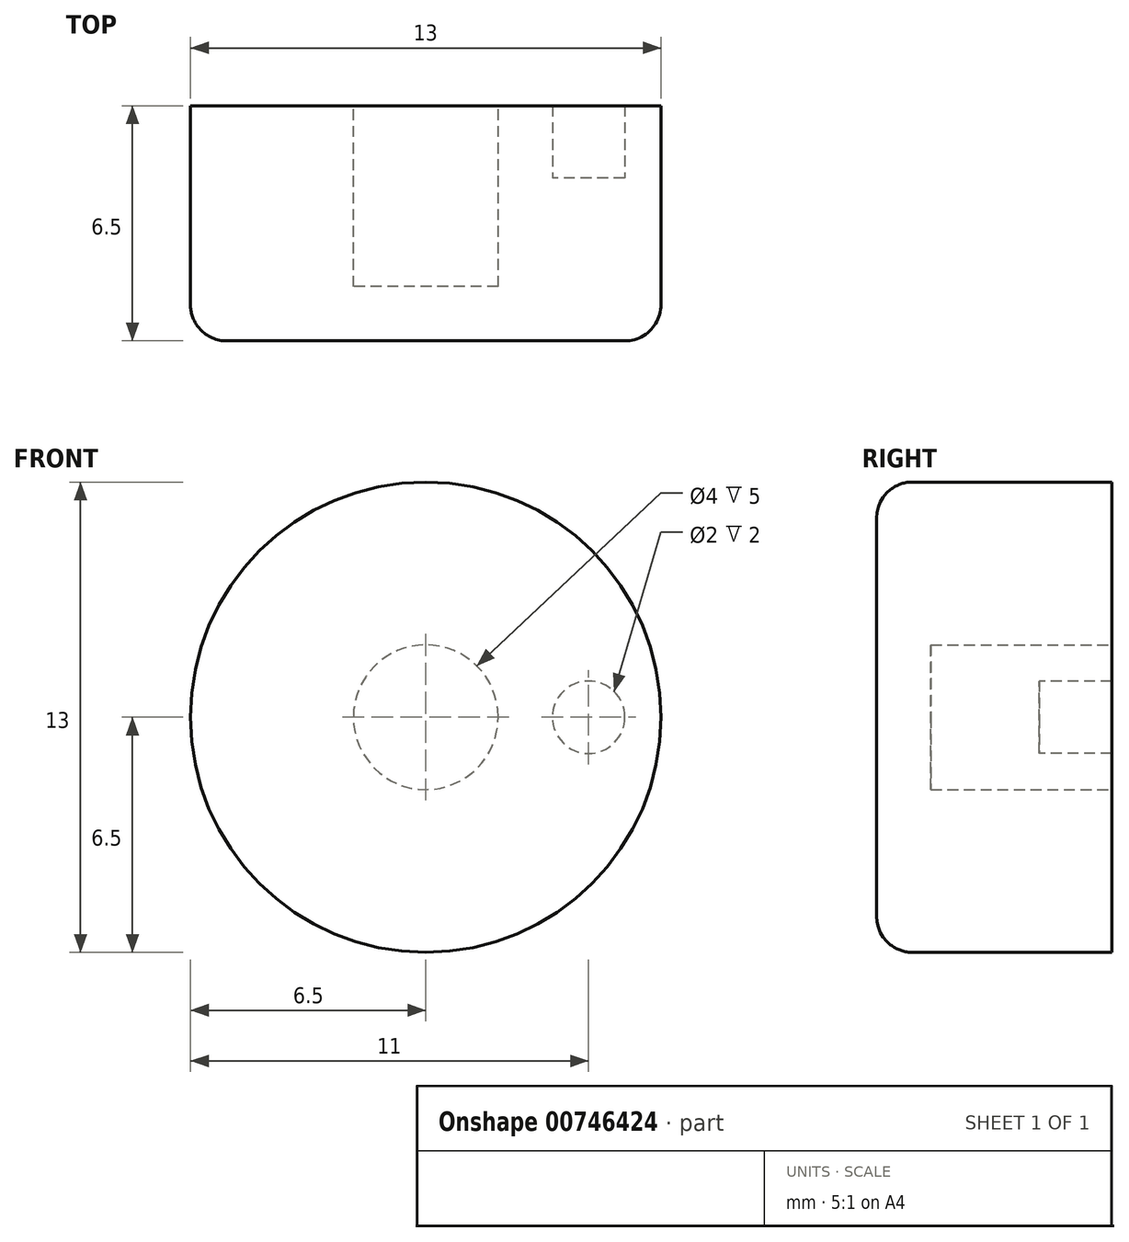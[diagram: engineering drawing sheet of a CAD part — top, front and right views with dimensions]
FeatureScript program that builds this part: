
annotation { "Feature Type Name" : "Feature", "Feature Type Description" : "" }
export const myFeature = defineFeature(function(context is Context, id is Id, definition is map)
    precondition{}
    {
        {
            var Q0;
            Q0=qCreatedBy(makeId("Top.planeOp"),FACE);
            var sketch = newSketch(context, id + "F0", { "sketchPlane" : qUnion([Q0])});
            skCircle(sketch, "E0", {"center": v(0, 0) * mm, "radius": 6.5 * mm});
            skSolve(sketch);
        }
        {
            var Q0;
            Q0=makeQuery(id+"F0.imprint","IMPRINT",FACE,{"disambiguationData":[TD([[makeQuery(id+"F0.imprint","IMPRINT",EDGE,{"derivedFrom":sQuery(id+"F0.wireOp",EDGE,"E0")}),1.0]])]});
            extrude(context, id + "F1", {"entities" : qUnion([Q0]), "depth" : 4.5 * mm, "offsetDistance" : 25.4 * mm});
        }
        {
            var Q0;
            Q0=makeQuery(id+"F1.opExtrude","CAP_FACE",FACE,{"disambiguationData":[OSD([sQuery(id+"F0.wireOp",EDGE,"E0")])],"isStart":false});
            var sketch = newSketch(context, id + "F2", { "sketchPlane" : qUnion([Q0])});
            skCircle(sketch, "E1", {"center": v(0, 0) * mm, "radius": 2 * mm});
            skSolve(sketch);
        }
        {
            var Q0;
            Q0 = qSketchRegion(id + "F2", true);
            extrude(context, id + "F3", {"entities" : qUnion([Q0]), "operationType" : NewBodyOperationType.REMOVE, "oppositeDirection" : true, "depth" : 3 * mm, "offsetDistance" : 25.4 * mm});
        }
        {
            var Q0;
            Q0=makeQuery(id+"F1.opExtrude","CAP_FACE",FACE,{"disambiguationData":[OSD([sQuery(id+"F0.wireOp",EDGE,"E0")])],"isStart":false});
            var sketch = newSketch(context, id + "F4", { "sketchPlane" : qUnion([Q0])});
            skPoint(sketch, "E2", {"position": v(-4.5, 0) * mm});
            skCircle(sketch, "E3", {"center": v(-4.5, 0) * mm, "radius": 1 * mm});
            skCircle(sketch, "E4.MirrorC", {"center": v(4.5, 0) * mm, "radius": 1 * mm});
            skSolve(sketch);
        }
        {
            var Q0;
            Q0=makeQuery(id+"F4.imprint","IMPRINT",FACE,{"disambiguationData":[TD([[makeQuery(id+"F4.imprint","IMPRINT",EDGE,{"derivedFrom":sQuery(id+"F4.wireOp",EDGE,"E3")}),1.0]])]});
            var Q1;
            Q1=makeQuery(id+"F4.imprint","IMPRINT",FACE,{"disambiguationData":[TD([[makeQuery(id+"F4.imprint","IMPRINT",EDGE,{"derivedFrom":sQuery(id+"F4.wireOp",EDGE,"E4.MirrorC")}),-1.0]])]});
            extrude(context, id + "F5", {"entities" : qUnion([Q0, Q1]), "operationType" : NewBodyOperationType.ADD, "depth" : 2 * mm, "offsetDistance" : 25.4 * mm});
        }
        {
            var Q0;
            Q0=makeQuery(id+"F1.opExtrude","CAP_EDGE",EDGE,{"disambiguationData":[OSD([sQuery(id+"F0.wireOp",EDGE,"E0")])],"isStart":true});
            fillet(context, id + "F6", {"entities" : qUnion([Q0]), "radius" : 1 * mm, "tangentPropagation" : true, "allowEdgeOverflow" : false});
        }
        {
            var Q0;
            Q0=qCreatedBy(makeId("Top.planeOp"),FACE);
            var sketch = newSketch(context, id + "F7", { "sketchPlane" : qUnion([Q0])});
            skLineSegment(sketch, "E5", {"start": v(-31.3, 0) * mm, "end": v(40.22, 0) * mm});
            skSolve(sketch);
        }
        {
            var Q0;
            Q0=makeQuery(id+"F1.opExtrude","SWEPT_BODY",BODY,{"disambiguationData":[OSD([sQuery(id+"F0.wireOp",EDGE,"E0")])]});
            var Q1;
            Q1=sQuery(id+"F7.wireOp",EDGE,"E5");
            transform(context, id + "F8", {"entities" : qUnion([Q0]), "transformType" : TransformType.ROTATION, "transformAxis" : qUnion([Q1]), "angle" : 90 * degree, "oppositeDirection" : true, "makeCopy" : false});
        }
    });
